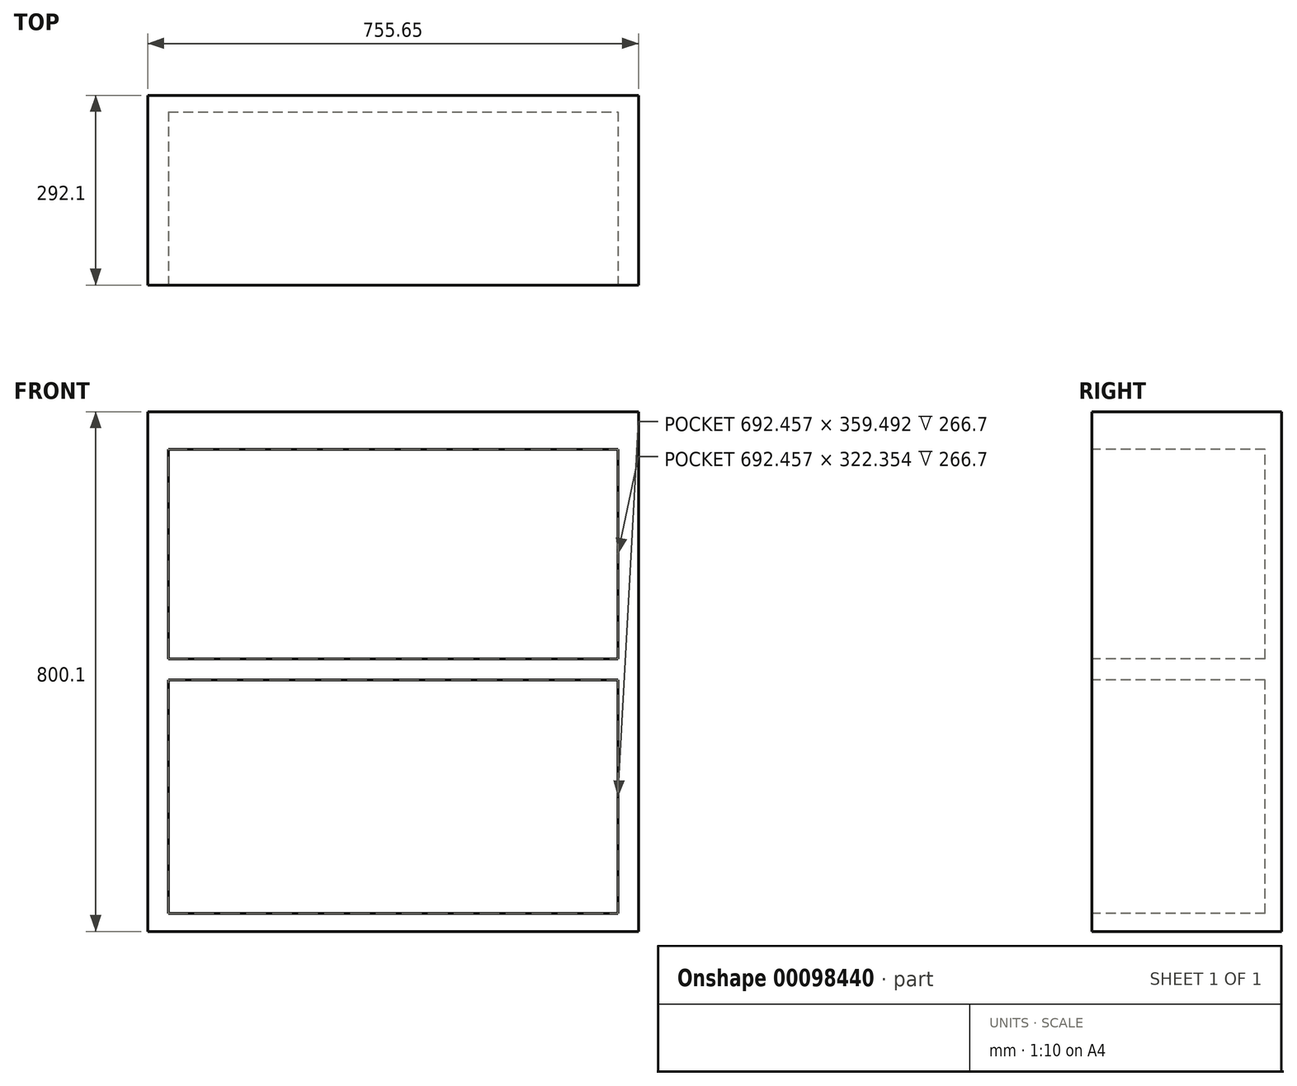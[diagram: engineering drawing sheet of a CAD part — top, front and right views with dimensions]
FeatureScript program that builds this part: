
annotation { "Feature Type Name" : "Feature", "Feature Type Description" : "" }
export const myFeature = defineFeature(function(context is Context, id is Id, definition is map)
    precondition{}
    {
        {
            var Q0;
            Q0=qCreatedBy(makeId("Top.planeOp"),FACE);
            var sketch = newSketch(context, id + "F0", { "sketchPlane" : qUnion([Q0])});
            skLineSegment(sketch, "E0.bottom", {"start": v(-375.69, -167.16) * mm, "end": v(379.96, -167.16) * mm});
            skLineSegment(sketch, "E0.top", {"start": v(-375.69, 124.94) * mm, "end": v(379.96, 124.94) * mm});
            skLineSegment(sketch, "E0.left", {"start": v(-375.69, -167.16) * mm, "end": v(-375.69, 124.94) * mm});
            skLineSegment(sketch, "E0.right", {"start": v(379.96, -167.16) * mm, "end": v(379.96, 124.94) * mm});
            skSolve(sketch);
        }
        {
            var Q0;
            Q0 = qSketchRegion(id + "F0", true);
            extrude(context, id + "F1", {"entities" : qUnion([Q0]), "depth" : 800.1 * mm});
        }
        {
            var Q0;
            Q0=makeQuery(id+"F1.opExtrude","SWEPT_FACE",FACE,{"disambiguationData":[OSD([sQuery(id+"F0.wireOp",EDGE,"E0.bottom")])]});
            var sketch = newSketch(context, id + "F2", { "sketchPlane" : qUnion([Q0])});
            skLineSegment(sketch, "E1.bottom", {"start": v(-343.75, 27.69) * mm, "end": v(348.7, 27.69) * mm});
            skLineSegment(sketch, "E1.top", {"start": v(-343.75, 387.18) * mm, "end": v(348.7, 387.18) * mm});
            skLineSegment(sketch, "E1.left", {"start": v(-343.75, 27.69) * mm, "end": v(-343.75, 387.18) * mm});
            skLineSegment(sketch, "E1.right", {"start": v(348.7, 27.69) * mm, "end": v(348.7, 387.18) * mm});
            skSolve(sketch);
        }
        {
            var Q0;
            Q0 = qSketchRegion(id + "F2", true);
            extrude(context, id + "F3", {"entities" : qUnion([Q0]), "operationType" : NewBodyOperationType.REMOVE, "oppositeDirection" : true, "depth" : 266.7 * mm});
        }
        {
            var Q0;
            Q0=makeQuery(id+"F1.opExtrude","SWEPT_FACE",FACE,{"disambiguationData":[OSD([sQuery(id+"F0.wireOp",EDGE,"E0.bottom")])]});
            var sketch = newSketch(context, id + "F4", { "sketchPlane" : qUnion([Q0])});
            skLineSegment(sketch, "E2.bottom", {"start": v(-343.75, 419.63) * mm, "end": v(348.7, 419.63) * mm});
            skLineSegment(sketch, "E2.top", {"start": v(-343.75, 741.99) * mm, "end": v(348.7, 741.99) * mm});
            skLineSegment(sketch, "E2.left", {"start": v(-343.75, 419.63) * mm, "end": v(-343.75, 741.99) * mm});
            skLineSegment(sketch, "E2.right", {"start": v(348.7, 419.63) * mm, "end": v(348.7, 741.99) * mm});
            skSolve(sketch);
        }
        {
            var Q0;
            Q0 = qSketchRegion(id + "F4", true);
            extrude(context, id + "F5", {"entities" : qUnion([Q0]), "operationType" : NewBodyOperationType.REMOVE, "oppositeDirection" : true, "depth" : 266.7 * mm});
        }
    });
